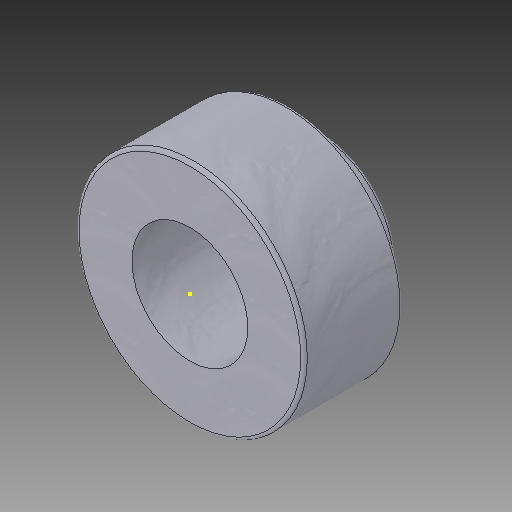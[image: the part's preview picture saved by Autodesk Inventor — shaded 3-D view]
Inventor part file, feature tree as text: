
AUTODESK INVENTOR PART (.ipt)
format: ipt  version: 2019 (Build 230136000, 136)  size: 207,872 bytes
history: native  units: in
note: dims shown in document units (in); Inventor stores cm internally (conversion verified against a paired STEP export)
features: sketch x6, other x3
ambient origin geometry x8: Origin, YZ Plane, XZ Plane, XY Plane, X Axis, Y Axis, Z Axis, Center Point
bodies: Solid1 (feature_tree)
feature tree (9):
  other  "project flange bearing part2_MIR1_MIR.ipt"
  other  "Solid1::project flange bearing part2_MIR1_MIR.ipt"
  other  "TaggingFeature1"
  sketch  "Sketch1"  dims[d0=0.3937in]
  sketch  "Sketch2"
  sketch  "Sketch3"
  sketch  "Sketch4"
  sketch  "Sketch5"
  sketch  "Sketch6"
